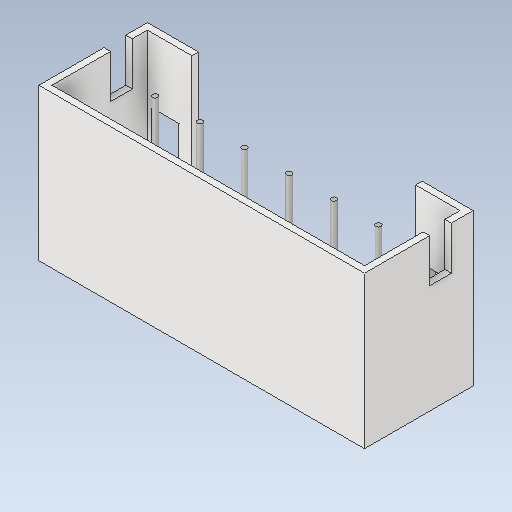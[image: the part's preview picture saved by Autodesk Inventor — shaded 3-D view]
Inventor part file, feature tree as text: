
AUTODESK INVENTOR PART (.ipt)
format: ipt  version: 2020 (Build 240168000, 168)  size: 202,240 bytes
history: native  units: mm
features: extrude x5, sketch x5, mirror x3, projected_geometry x3, pattern_linear x1
ambient origin geometry x8: Origin, YZ Plane, XZ Plane, XY Plane, X Axis, Y Axis, Z Axis, Center Point
bodies: Solid1 (feature_tree)
feature tree (17):
  extrude  "Extrusion1"  Depth=5.0mm
  extrude  "Extrusion2"  Depth=0.3mm
  mirror  "Mirror1"
  extrude  "Extrusion3"  Depth=0.3mm
  mirror  "Mirror2"
  extrude  "Extrusion4"  Depth=1.25mm
  pattern_linear  "Rectangular Pattern1"  Spacing1=0.5mm  [1 undecoded]
  extrude  "Extrusion5"  Depth=0.5mm
  mirror  "Mirror3"
  sketch  "Sketch1"  dims[d0=15.0mm d1=5.0mm]
  sketch  "Sketch2"  dims[d2=1.0mm d3=0.0mm d4=0.3mm]
  projected_geometry  "Projected Loop1"
  sketch  "Sketch3"  dims[d5=0.3mm d6=0.3mm]
  projected_geometry  "Projected Loop2"
  sketch  "Sketch4"  dims[d7=6.0mm d8=0.0mm d9=1.25mm]
  sketch  "Sketch5"  dims[d10=2.5mm d11=0.5mm d12=0.5mm d13=6.0mm d14=0.0mm d15=0.25mm d16=0.5mm d17=14.4mm d18=2.057143mm d19=5.25mm d20=0.0mm d21=60.0mm d23=2.057143mm d24=2.625mm d25=0.0mm d26=1.0mm d27=2.0mm d28=1.0mm d29=5.25mm d30=0.0mm]
  projected_geometry  "Projected Loop3"
note: 1 required parameter value undecoded (feature->parameter linkage not recoverable at this tier; creation-order binding heuristic only, values carry confidence <= 0.55)
